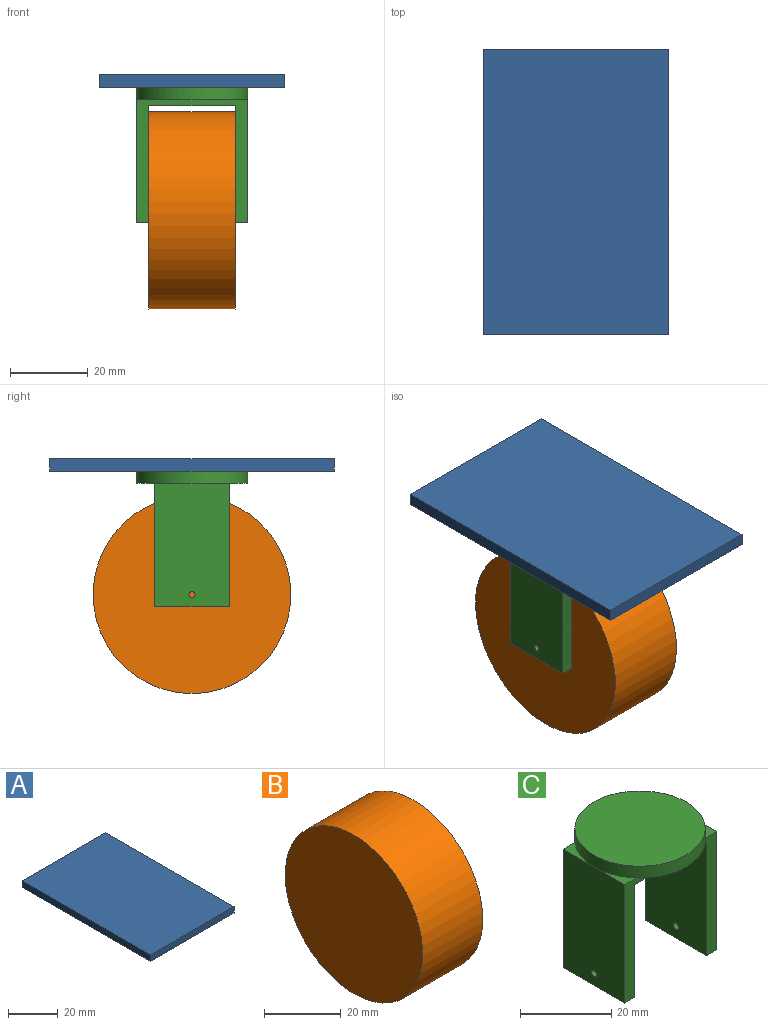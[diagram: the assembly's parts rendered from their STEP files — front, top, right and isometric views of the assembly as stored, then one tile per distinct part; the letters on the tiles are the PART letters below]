
ASSEMBLY  parts=3 mates=2
PART A: 6 faces, bbox 47.6x73x3.2 mm
  f0: plane 73.03x3.18mm, normal (1,0,0), area 231.9mm2, adj f1,f3,f4,f5
  f1: plane 47.63x3.18mm, normal (0,1,0), area 151.2mm2, adj f0,f2,f4,f5
  f2: plane 73.03x3.18mm, normal (-1,0,0), area 231.9mm2, adj f1,f3,f4,f5
  f3: plane 47.63x3.18mm, normal (0,-1,0), area 151.2mm2, adj f0,f2,f4,f5
  f4: plane 73.03x47.63mm, normal (0,0,-1), area 3477.8mm2, adj f0,f1,f2,f3
  f5: plane 73.03x47.63mm, normal (0,0,1), area 3477.8mm2, adj f0,f1,f2,f3
PART B: 3 faces, bbox 22.2x50.8x50.8 mm
  f0: cylinder r=25.4mm len=50.8mm, axis (1,0,0), area 3547mm2, adj f1,f2
  f1: plane 50.8x50.8mm, normal (-1,0,0), area 2026.8mm2, adj f0
  f2: plane 50.8x50.8mm, normal (1,0,0), area 2026.8mm2, adj f0
PART C: 19 faces, bbox 28.6x28.6x34.9 mm
  f0: plane 19.05x3.18mm, normal (0,0,-1), area 60.5mm2, adj f1,f2,f8,f16
  f1: plane 31.75x28.58mm, normal (0,-1,0), area 236.9mm2, adj f0,f4,f6,f7,f8,f9,f10,f14
  f2: plane 31.75x28.58mm, normal (0,1,0), area 236.9mm2, adj f0,f3,f5,f7,f8,f9,f13,f14
  f3: plane 9.53x3.64mm, normal (0,0,1), area 10.9mm2, adj f2,f8,f11
  f4: plane 9.53x3.64mm, normal (0,0,1), area 10.9mm2, adj f1,f8,f11
  f5: plane 9.53x3.64mm, normal (0,0,1), area 10.9mm2, adj f2,f9,f11
  f6: plane 9.53x3.64mm, normal (0,0,1), area 10.9mm2, adj f1,f9,f11
  f7: plane 19.05x3.18mm, normal (0,0,-1), area 60.5mm2, adj f1,f2,f9,f14
  f8: plane 31.75x19.05mm, normal (-1,0,0), area 602.9mm2, adj f0,f1,f2,f3,f4,f17
  f9: plane 31.75x19.05mm, normal (1,0,0), area 602.9mm2, adj f1,f2,f5,f6,f7,f18
  f10: plane 21.3x4.76mm, normal (0,0,-1), area 70.3mm2, adj f1,f11
  f11: cylinder r=14.29mm len=28.58mm, axis (0,0,-1), area 285mm2, adj f3,f4,f5,f6,f10,f12,f13
  f12: plane 28.58x28.58mm, normal (0,0,1), area 641.3mm2, adj f11
  f13: plane 21.3x4.76mm, normal (0,0,-1), area 70.3mm2, adj f2,f11
  f14: plane 30.16x19.05mm, normal (-1,0,0), area 572.6mm2, adj f1,f2,f7,f15,f18
  f15: plane 22.23x19.05mm, normal (0,0,-1), area 423.4mm2, adj f1,f2,f14,f16
  f16: plane 30.16x19.05mm, normal (1,0,0), area 572.6mm2, adj f0,f1,f2,f15,f17
  f17: cylinder r=0.79mm len=3.18mm, axis (1,0,0), area 15.8mm2, adj f8,f16
  f18: cylinder r=0.79mm len=3.18mm, axis (1,0,0), area 15.8mm2, adj f9,f14
PLACE A at identity
PLACE B at identity
PLACE C at identity
MATE revolute A.f4 <-> C.f11  axis (0,0,-1) through (0,0,-3.18)mm
MATE revolute B.f0 <-> C.f17  axis (1,0,0) through (11.11,0,-34.93)mm
